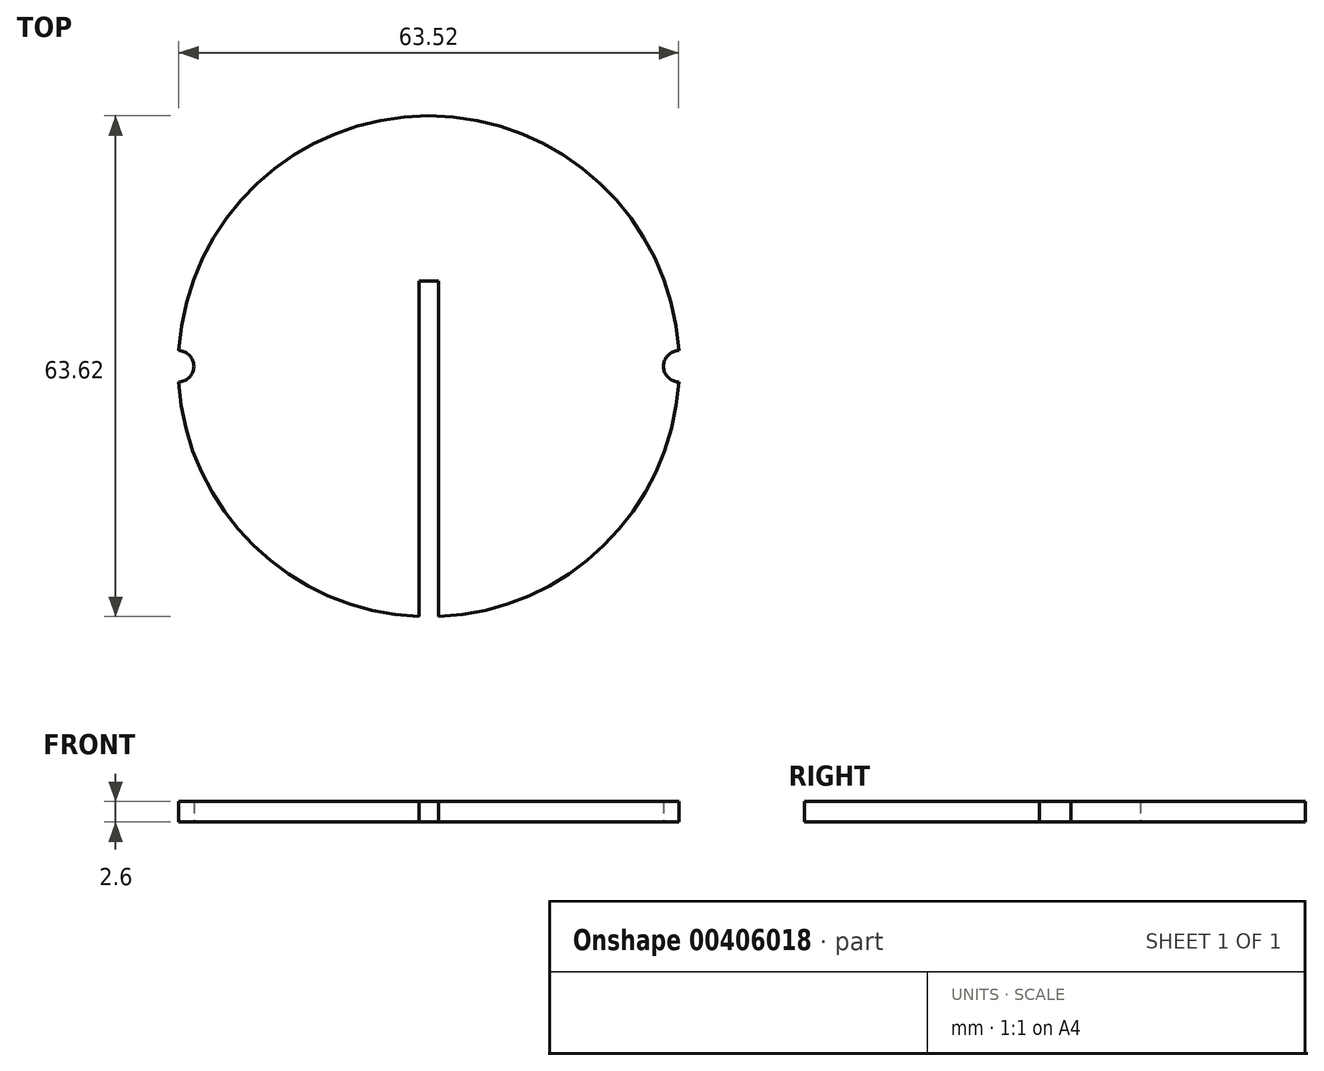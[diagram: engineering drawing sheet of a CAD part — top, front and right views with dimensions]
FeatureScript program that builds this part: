
annotation { "Feature Type Name" : "Feature", "Feature Type Description" : "" }
export const myFeature = defineFeature(function(context is Context, id is Id, definition is map)
    precondition{}
    {
        {
            var Q0;
            Q0=qCreatedBy(makeId("Top.planeOp"),FACE);
            var sketch = newSketch(context, id + "F0", { "sketchPlane" : qUnion([Q0])});
            skCircle(sketch, "E0", {"center": v(0, 0) * mm, "radius": 31.82 * mm});
            skLineSegment(sketch, "E1.bottom", {"start": v(-1.25, 10.82) * mm, "end": v(1.25, 10.82) * mm});
            skLineSegment(sketch, "E1.top", {"start": v(-1.25, -31.82) * mm, "end": v(1.25, -31.82) * mm});
            skLineSegment(sketch, "E1.left", {"start": v(-1.25, 10.82) * mm, "end": v(-1.25, -31.82) * mm});
            skLineSegment(sketch, "E1.right", {"start": v(1.25, 10.82) * mm, "end": v(1.25, -31.82) * mm});
            skPoint(sketch, "E2", {"position": v(0, 10.82) * mm});
            skCircle(sketch, "E3", {"center": v(-31.82, 0) * mm, "radius": 2 * mm});
            skCircle(sketch, "E4", {"center": v(31.82, 0) * mm, "radius": 2 * mm});
            skSolve(sketch);
        }
        {
            var Q0;
            {var subQ0=sQuery(id+"F0.wireOp",EDGE,"E1.bottom");Q0=makeQuery(id+"F0.imprint","IMPRINT",FACE,{"disambiguationData":[TD([[makeQuery(id+"F0.imprint","IMPRINT",EDGE,{"derivedFrom":subQ0}),1.0]])]});}
            extrude(context, id + "F1", {"entities" : qUnion([Q0]), "depth" : 2.6 * mm});
        }
    });
